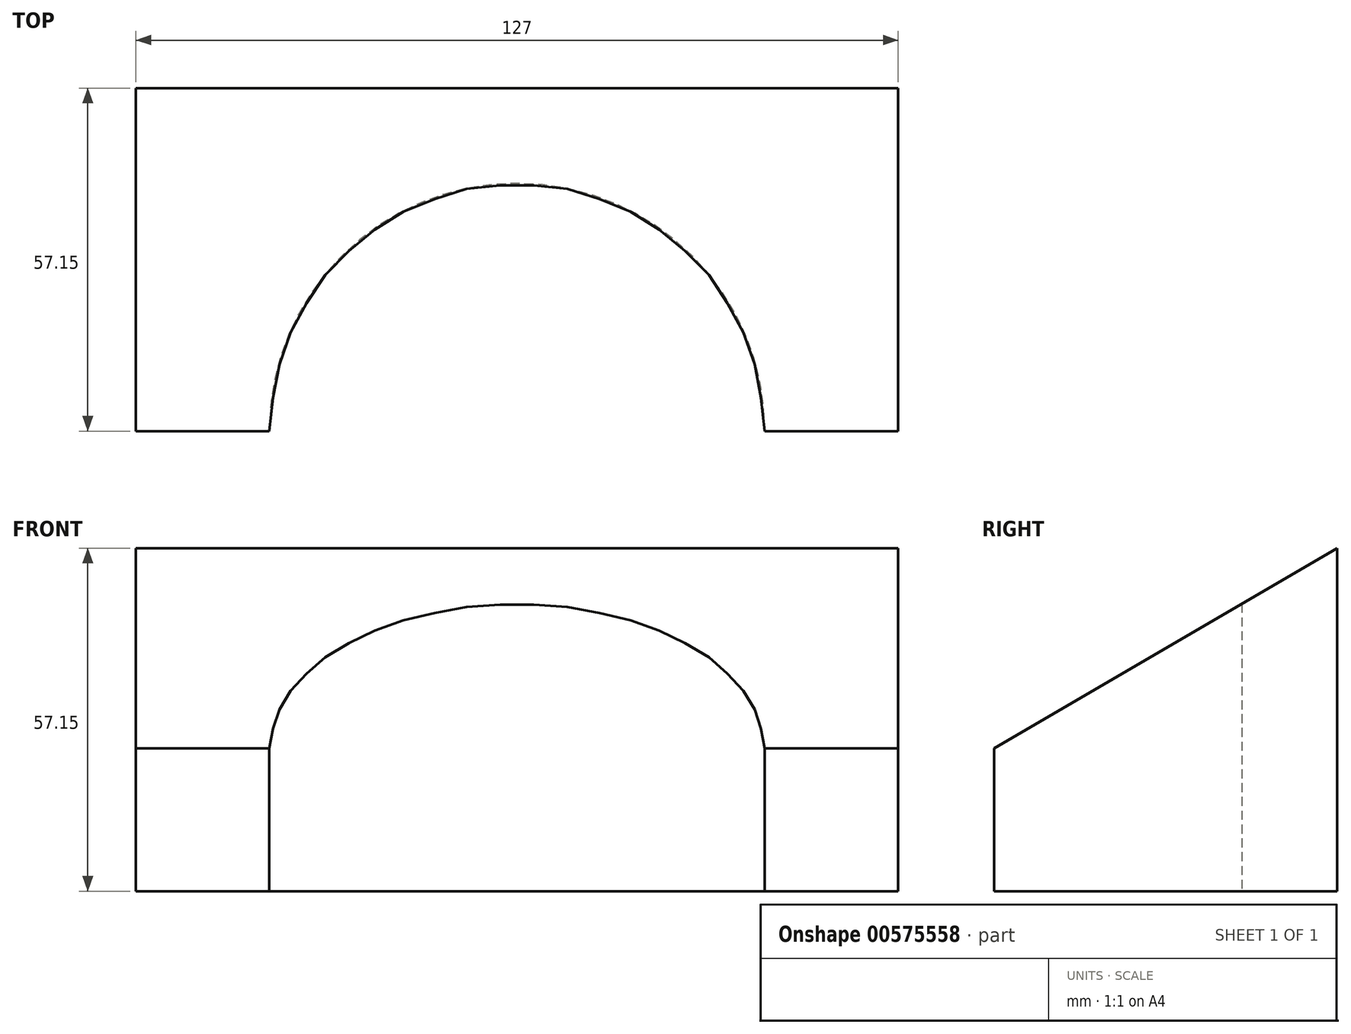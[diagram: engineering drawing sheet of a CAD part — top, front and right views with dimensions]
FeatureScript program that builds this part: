
annotation { "Feature Type Name" : "Feature", "Feature Type Description" : "" }
export const myFeature = defineFeature(function(context is Context, id is Id, definition is map)
    precondition{}
    {
        {
            var Q0;
            Q0=qCreatedBy(makeId("Right.planeOp"),FACE);
            var sketch = newSketch(context, id + "F0", { "sketchPlane" : qUnion([Q0])});
            skLineSegment(sketch, "E0", {"start": v(-15.98, 4.49) * mm, "end": v(-15.98, -19.33) * mm});
            skLineSegment(sketch, "E1", {"start": v(-15.98, -19.33) * mm, "end": v(41.17, -19.33) * mm});
            skLineSegment(sketch, "E2", {"start": v(41.17, -19.33) * mm, "end": v(41.17, 37.82) * mm});
            skLineSegment(sketch, "E3", {"start": v(41.17, 37.82) * mm, "end": v(-15.98, 4.49) * mm});
            skSolve(sketch);
        }
        {
            var Q0;
            Q0=makeQuery(id+"F0.imprint","IMPRINT",FACE,{"disambiguationData":[TD([[makeQuery(id+"F0.imprint","IMPRINT",EDGE,{"derivedFrom":sQuery(id+"F0.wireOp",EDGE,"E0")}),1.0]])]});
            extrude(context, id + "F1", {"entities" : qUnion([Q0]), "depth" : 127 * mm, "offsetDistance" : 25.4 * mm});
        }
        {
            var Q0;
            Q0=makeQuery(id+"F1.opExtrude","SWEPT_FACE",FACE,{"disambiguationData":[OSD([sQuery(id+"F0.wireOp",EDGE,"E1")])]});
            var sketch = newSketch(context, id + "F2", { "sketchPlane" : qUnion([Q0])});
            skArc(sketch, "E4", {"start": v(22.22, 15.98) * mm, "mid": v(63.5, -25.3) * mm, "end": v(104.78, 15.98) * mm});
            skSolve(sketch);
        }
        {
            var Q0;
            {var subQ0=sQuery(id+"F2.wireOp",EDGE,"E4");Q0=makeQuery(id+"F2.imprint","IMPRINT",FACE,{"disambiguationData":[TD([[makeQuery(id+"F2.imprint","IMPRINT",EDGE,{"derivedFrom":subQ0}),1.0]])]});}
            extrude(context, id + "F3", {"entities" : qUnion([Q0]), "operationType" : NewBodyOperationType.REMOVE, "oppositeDirection" : true, "depth" : 127 * mm, "offsetDistance" : 25.4 * mm});
        }
    });
